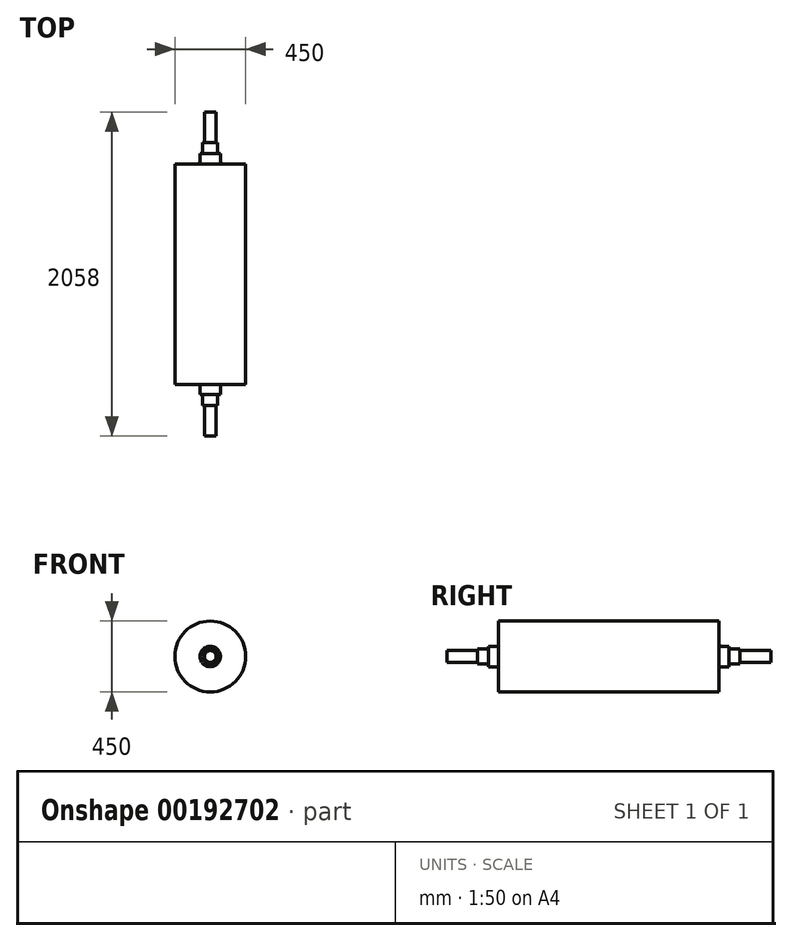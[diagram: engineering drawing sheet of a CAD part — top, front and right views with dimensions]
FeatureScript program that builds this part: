
annotation { "Feature Type Name" : "Feature", "Feature Type Description" : "" }
export const myFeature = defineFeature(function(context is Context, id is Id, definition is map)
    precondition{}
    {
        {
            var Q0;
            Q0=qCreatedBy(makeId("Right.planeOp"),FACE);
            var sketch = newSketch(context, id + "F0", { "sketchPlane" : qUnion([Q0])});
            skLineSegment(sketch, "E0", {"start": v(0, 80) * mm, "end": v(0, 225) * mm});
            skLineSegment(sketch, "E1", {"start": v(0, 225) * mm, "end": v(-150, 225) * mm});
            skLineSegment(sketch, "E2", {"start": v(-200, 224.93) * mm, "end": v(-150, 225) * mm});
            skLineSegment(sketch, "E3", {"start": v(-200, 224.93) * mm, "end": v(-700, 224.93) * mm});
            skLineSegment(sketch, "E4", {"start": v(0, 0) * mm, "end": v(-700, 0) * mm});
            skLineSegment(sketch, "E5.MirrorCS", {"start": v(-1200, 224.93) * mm, "end": v(-700, 224.93) * mm});
            skLineSegment(sketch, "E6.MirrorCS", {"start": v(-1200, 224.93) * mm, "end": v(-1250, 225) * mm});
            skLineSegment(sketch, "E7.MirrorCS", {"start": v(-1400, 225) * mm, "end": v(-1250, 225) * mm});
            skLineSegment(sketch, "E8.MirrorCS", {"start": v(-1400, 0) * mm, "end": v(-1400, 225) * mm});
            skLineSegment(sketch, "E9.MirrorCS", {"start": v(-1400, 0) * mm, "end": v(-700, 0) * mm});
            skLineSegment(sketch, "E10", {"start": v(0, 0) * mm, "end": v(64, 0) * mm});
            skLineSegment(sketch, "E11", {"start": v(64, 0) * mm, "end": v(64, 65) * mm});
            skLineSegment(sketch, "E12", {"start": v(64, 65) * mm, "end": v(15, 65) * mm});
            skPoint(sketch, "E13.newPointA", {"position": v(0, 0) * mm});
            skArc(sketch, "E13.filletArc", {"start": v(0, 80) * mm, "mid": v(4.4, 69.4) * mm, "end": v(15, 65) * mm});
            skLineSegment(sketch, "E14", {"start": v(64, 0) * mm, "end": v(134, 0) * mm});
            skLineSegment(sketch, "E15", {"start": v(134, 0) * mm, "end": v(134, 47.5) * mm});
            skLineSegment(sketch, "E16", {"start": v(134, 47.5) * mm, "end": v(64, 47.5) * mm});
            skLineSegment(sketch, "E17", {"start": v(134, 0) * mm, "end": v(329, 0) * mm});
            skLineSegment(sketch, "E18", {"start": v(329, 0) * mm, "end": v(329, 37.5) * mm});
            skLineSegment(sketch, "E19", {"start": v(329, 37.5) * mm, "end": v(134, 37.5) * mm});
            skLineSegment(sketch, "E20", {"start": v(-700, 224.93) * mm, "end": v(-700, 0) * mm});
            skLineSegment(sketch, "E21.MirrorCS", {"start": v(-1729, 0) * mm, "end": v(-1729, 37.5) * mm});
            skLineSegment(sketch, "E22.MirrorCS", {"start": v(-1534, 0) * mm, "end": v(-1534, 47.5) * mm});
            skLineSegment(sketch, "E23.MirrorCS", {"start": v(-1534, 47.5) * mm, "end": v(-1464, 47.5) * mm});
            skLineSegment(sketch, "E24.MirrorCS", {"start": v(-1729, 37.5) * mm, "end": v(-1534, 37.5) * mm});
            skLineSegment(sketch, "E25.MirrorCS", {"start": v(-1464, 0) * mm, "end": v(-1464, 65) * mm});
            skLineSegment(sketch, "E26.MirrorCS", {"start": v(-1534, 0) * mm, "end": v(-1729, 0) * mm});
            skLineSegment(sketch, "E27.MirrorCS", {"start": v(-1464, 0) * mm, "end": v(-1534, 0) * mm});
            skArc(sketch, "E28.MirrorCS", {"start": v(-1400, 80) * mm, "mid": v(-1404.4, 69.4) * mm, "end": v(-1415, 65) * mm});
            skLineSegment(sketch, "E29.MirrorCS", {"start": v(-1400, 0) * mm, "end": v(-1464, 0) * mm});
            skLineSegment(sketch, "E30.MirrorCS", {"start": v(-1464, 65) * mm, "end": v(-1415, 65) * mm});
            skPoint(sketch, "E31.MirrorP", {"position": v(-1400, 0) * mm});
            skSolve(sketch);
        }
        {
            var Q0;
            Q0 = qSketchRegion(id + "F0", true);
            var Q1;
            Q1=sQuery(id+"F0.wireOp",EDGE,"E4");
            revolve(context, id + "F1", {"entities" : qUnion([Q0]), "axis" : qUnion([Q1]), "revolveType" : RevolveType.FULL});
        }
    });
